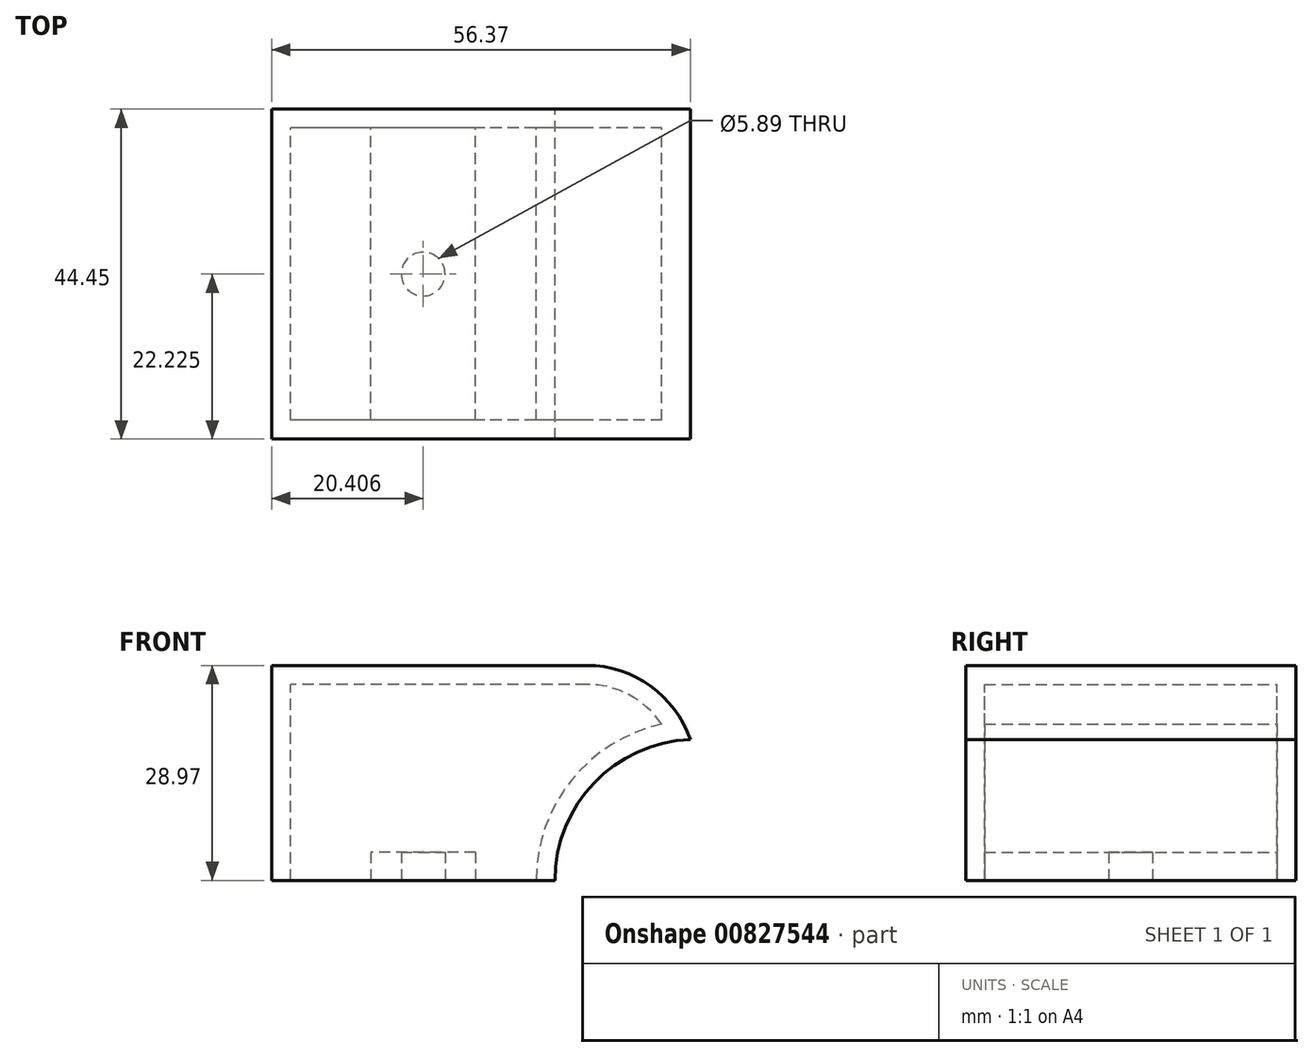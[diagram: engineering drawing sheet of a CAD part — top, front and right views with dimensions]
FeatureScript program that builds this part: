
annotation { "Feature Type Name" : "Feature", "Feature Type Description" : "" }
export const myFeature = defineFeature(function(context is Context, id is Id, definition is map)
    precondition{}
    {
        {
            var Q0;
            Q0=qCreatedBy(makeId("Front.planeOp"),FACE);
            var sketch = newSketch(context, id + "F0", { "sketchPlane" : qUnion([Q0])});
            skLineSegment(sketch, "E0.bottom", {"start": v(0, 0) * mm, "end": v(-57.15, 0) * mm});
            skLineSegment(sketch, "E0.top", {"start": v(0, 28.97) * mm, "end": v(-57.15, 28.97) * mm});
            skLineSegment(sketch, "E0.left", {"start": v(0, 0) * mm, "end": v(0, 28.97) * mm});
            skLineSegment(sketch, "E0.right", {"start": v(-57.15, 0) * mm, "end": v(-57.15, 28.97) * mm});
            skSolve(sketch);
        }
        {
            var Q0;
            Q0=makeQuery(id+"F0.imprint","IMPRINT",FACE,{"disambiguationData":[TD([[makeQuery(id+"F0.imprint","IMPRINT",EDGE,{"derivedFrom":sQuery(id+"F0.wireOp",EDGE,"E0.bottom")}),-1.0]])]});
            extrude(context, id + "F1", {"entities" : qUnion([Q0]), "depth" : 44.45 * mm, "offsetDistance" : 25.4 * mm});
        }
        {
            var Q0;
            Q0=makeQuery(id+"F1.opExtrude","SWEPT_EDGE",EDGE,{"disambiguationData":[OSD([sQuery(id+"F0.wireOp",EDGE,"E0.top"),sQuery(id+"F0.wireOp",EDGE,"E0.left")])]});
            fillet(context, id + "F2", {"entities" : qUnion([Q0]), "radius" : 14.72 * mm, "tangentPropagation" : true, "allowEdgeOverflow" : false});
        }
        {
            var Q0;
            Q0=qCreatedBy(makeId("Front.planeOp"),FACE);
            var sketch = newSketch(context, id + "F3", { "sketchPlane" : qUnion([Q0])});
            skCircle(sketch, "E1", {"center": v(0, 0) * mm, "radius": 19 * mm});
            skSolve(sketch);
        }
        {
            var Q0;
            Q0 = qSketchRegion(id + "F3", true);
            extrude(context, id + "F4", {"entities" : qUnion([Q0]), "operationType" : NewBodyOperationType.REMOVE, "depth" : 66.55 * mm, "offsetDistance" : 25.4 * mm});
        }
        {
            var Q0;
            Q0=makeQuery(id+"F1.opExtrude","SWEPT_FACE",FACE,{"disambiguationData":[OSD([sQuery(id+"F0.wireOp",EDGE,"E0.bottom")])]});
            shell(context, id + "F5", {"entities" : qUnion([Q0]), "thickness" : 2.54 * mm});
        }
        {
            var Q0;
            Q0=makeQuery(id+"F1.opExtrude","SWEPT_FACE",FACE,{"disambiguationData":[OSD([sQuery(id+"F0.wireOp",EDGE,"E0.bottom")])]});
            var sketch = newSketch(context, id + "F6", { "sketchPlane" : qUnion([Q0])});
            skLineSegment(sketch, "E2.bottom", {"start": v(-43.8, 44.45) * mm, "end": v(-29.69, 44.45) * mm});
            skLineSegment(sketch, "E2.top", {"start": v(-43.8, 0) * mm, "end": v(-29.69, 0) * mm});
            skLineSegment(sketch, "E2.left", {"start": v(-43.8, 44.45) * mm, "end": v(-43.8, 0) * mm});
            skLineSegment(sketch, "E2.right", {"start": v(-29.69, 44.45) * mm, "end": v(-29.69, 0) * mm});
            skCircle(sketch, "E3", {"center": v(-36.74, 22.23) * mm, "radius": 2.95 * mm});
            skPoint(sketch, "E3.centerSnap0", {"position": v(-29.69, 22.23) * mm});
            skPoint(sketch, "E3.centerSnap1", {"position": v(-36.74, 44.45) * mm});
            skSolve(sketch);
        }
        {
            var Q0;
            Q0=makeQuery(id+"F6.imprint","IMPRINT",FACE,{"disambiguationData":[TD([[makeQuery(id+"F6.imprint","IMPRINT",EDGE,{"derivedFrom":sQuery(id+"F6.wireOp",EDGE,"E3")}),-1.0]])]});
            extrude(context, id + "F7", {"entities" : qUnion([Q0]), "operationType" : NewBodyOperationType.ADD, "oppositeDirection" : true, "depth" : 3.8 * mm, "offsetDistance" : 25.4 * mm});
        }
    });
